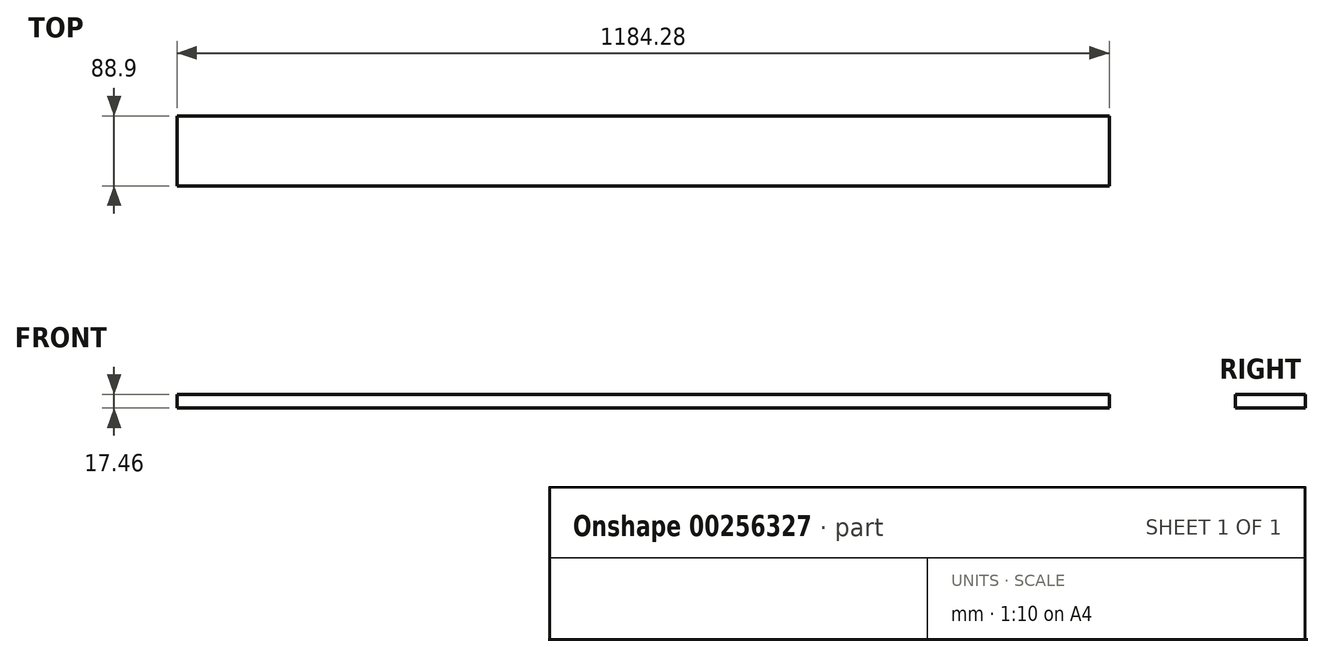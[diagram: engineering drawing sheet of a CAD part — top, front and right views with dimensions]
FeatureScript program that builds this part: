
annotation { "Feature Type Name" : "Feature", "Feature Type Description" : "" }
export const myFeature = defineFeature(function(context is Context, id is Id, definition is map)
    precondition{}
    {
        {
            var Q0;
            Q0=qCreatedBy(makeId("Right.planeOp"),FACE);
            var sketch = newSketch(context, id + "F0", { "sketchPlane" : qUnion([Q0])});
            skLineSegment(sketch, "E0.bottom", {"start": v(-44.45, 8.73) * mm, "end": v(44.45, 8.73) * mm});
            skLineSegment(sketch, "E0.top", {"start": v(-44.45, -8.73) * mm, "end": v(44.45, -8.73) * mm});
            skLineSegment(sketch, "E0.left", {"start": v(-44.45, 8.73) * mm, "end": v(-44.45, -8.73) * mm});
            skLineSegment(sketch, "E0.right", {"start": v(44.45, 8.73) * mm, "end": v(44.45, -8.73) * mm});
            skSolve(sketch);
        }
        {
            var Q0;
            Q0=qSketchRegion(id+"F0",true);
            extrude(context, id + "F1", {"entities" : qUnion([Q0]), "endBound" : BoundingType.SYMMETRIC, "depth" : 1184.27 * mm});
        }
    });
